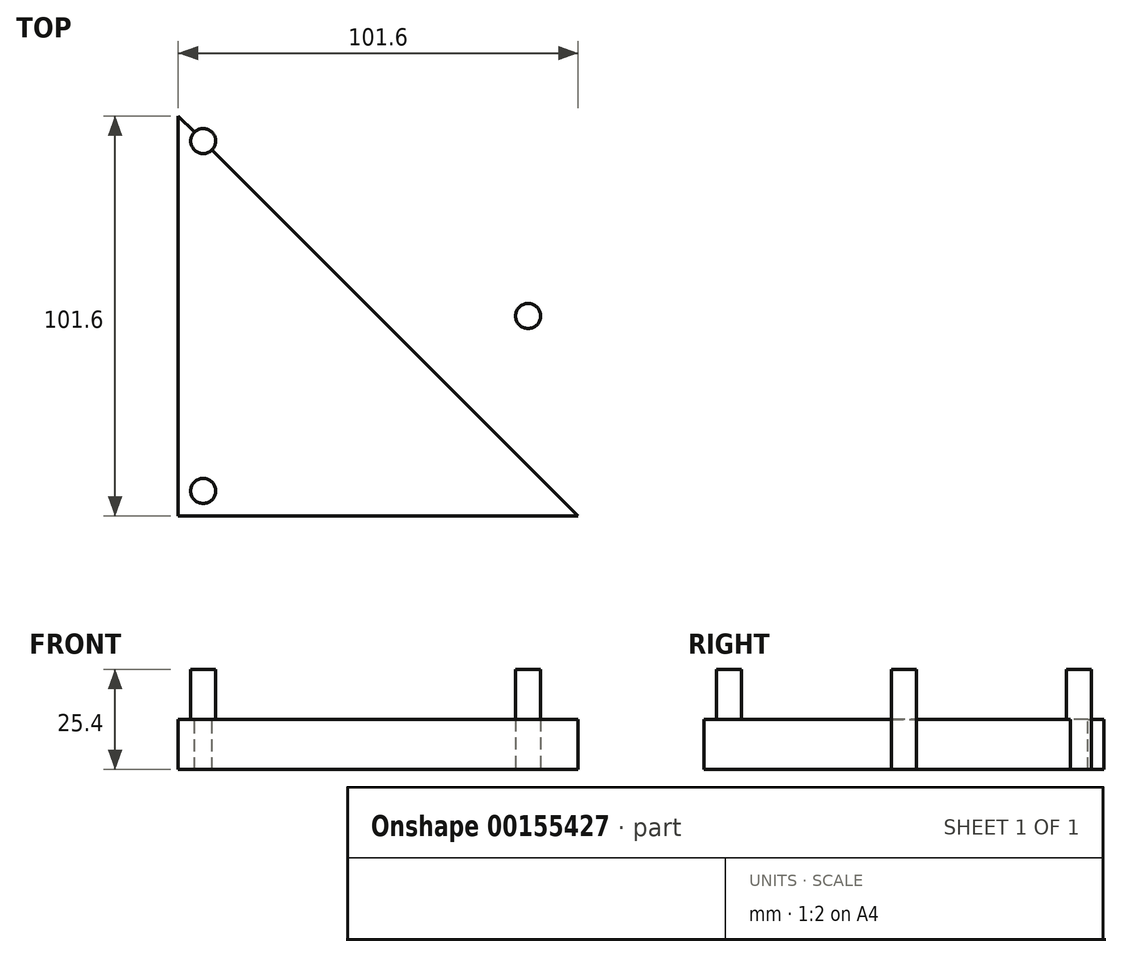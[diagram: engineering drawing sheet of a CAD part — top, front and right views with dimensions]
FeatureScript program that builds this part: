
annotation { "Feature Type Name" : "Feature", "Feature Type Description" : "" }
export const myFeature = defineFeature(function(context is Context, id is Id, definition is map)
    precondition{}
    {
        {
            var Q0;
            Q0=qCreatedBy(makeId("Top.planeOp"),FACE);
            var sketch = newSketch(context, id + "F0", { "sketchPlane" : qUnion([Q0])});
            skLineSegment(sketch, "E0.bottom", {"start": v(0, 0) * mm, "end": v(-101.6, 0) * mm});
            skLineSegment(sketch, "E0.top", {"start": v(0, -101.6) * mm, "end": v(-101.6, -101.6) * mm});
            skLineSegment(sketch, "E0.left", {"start": v(0, 0) * mm, "end": v(0, -101.6) * mm});
            skLineSegment(sketch, "E0.right", {"start": v(-101.6, 0) * mm, "end": v(-101.6, -101.6) * mm});
            skSolve(sketch);
        }
        {
            var Q0;
            Q0=makeQuery(id+"F0.imprint","IMPRINT",FACE,{"disambiguationData":[TD([[makeQuery(id+"F0.imprint","IMPRINT",EDGE,{"derivedFrom":sQuery(id+"F0.wireOp",EDGE,"E0.bottom")}),1.0]])]});
            extrude(context, id + "F1", {"entities" : qUnion([Q0]), "depth" : 12.7 * mm});
        }
        {
            var Q0;
            Q0=makeQuery(id+"F1.opExtrude","CAP_FACE",FACE,{"disambiguationData":[OSD([sQuery(id+"F0.wireOp",EDGE,"E0.bottom"),sQuery(id+"F0.wireOp",EDGE,"E0.top"),sQuery(id+"F0.wireOp",EDGE,"E0.left"),sQuery(id+"F0.wireOp",EDGE,"E0.right")])],"isStart":false});
            var sketch = newSketch(context, id + "F2", { "sketchPlane" : qUnion([Q0])});
            skLineSegment(sketch, "E1.bottom", {"start": v(-101.6, -101.6) * mm, "end": v(-88.9, -101.6) * mm});
            skLineSegment(sketch, "E1.top", {"start": v(-101.6, -88.9) * mm, "end": v(-88.9, -88.9) * mm});
            skLineSegment(sketch, "E1.left", {"start": v(-101.6, -101.6) * mm, "end": v(-101.6, -88.9) * mm});
            skLineSegment(sketch, "E1.right", {"start": v(-88.9, -101.6) * mm, "end": v(-88.9, -88.9) * mm});
            skLineSegment(sketch, "E2", {"start": v(-101.6, -88.9) * mm, "end": v(-88.9, -101.6) * mm});
            skLineSegment(sketch, "E3", {"start": v(-101.6, -101.6) * mm, "end": v(-88.9, -88.9) * mm});
            skPoint(sketch, "E4", {"position": v(-95.25, -95.25) * mm});
            skPoint(sketch, "E5.1.0.0", {"position": v(-69.85, -95.25) * mm});
            skPoint(sketch, "E5.2.0.0", {"position": v(-44.45, -95.25) * mm});
            skLineSegment(sketch, "E5.direction1", {"start": v(-95.25, -95.25) * mm, "end": v(-69.85, -95.25) * mm, "construction": true});
            skLineSegment(sketch, "E6.bottom", {"start": v(-101.6, 0) * mm, "end": v(-88.9, 0) * mm});
            skLineSegment(sketch, "E6.top", {"start": v(-101.6, -12.7) * mm, "end": v(-88.9, -12.7) * mm});
            skLineSegment(sketch, "E6.left", {"start": v(-101.6, 0) * mm, "end": v(-101.6, -12.7) * mm});
            skLineSegment(sketch, "E6.right", {"start": v(-88.9, 0) * mm, "end": v(-88.9, -12.7) * mm});
            skPoint(sketch, "E7", {"position": v(-95.25, -6.35) * mm});
            skPoint(sketch, "E7.positionSnap0", {"position": v(-95.25, -12.7) * mm});
            skPoint(sketch, "E7.positionSnap1", {"position": v(-101.6, -6.35) * mm});
            skCircle(sketch, "E8", {"center": v(-95.25, -95.25) * mm, "radius": 3.18 * mm});
            skCircle(sketch, "E9", {"center": v(-95.25, -6.35) * mm, "radius": 3.18 * mm});
            skSolve(sketch);
        }
        {
            var Q0;
            {var subQ0=sQuery(id+"F2.wireOp",EDGE,"E3");var subQ1=sQuery(id+"F2.wireOp",EDGE,"E2");var subQ2=makeQuery(id+"F2.imprint","INTERSECT",VERTEX,{"derivedFrom":[subQ1,subQ0]});Q0=makeQuery(id+"F2.imprint","IMPRINT",FACE,{"disambiguationData":[TD([[makeQuery(id+"F2.imprint","IMPRINT",EDGE,{"disambiguationData":[TD([[subQ2,-1.0]])],"derivedFrom":subQ1}),-1.0]])]});}
            var Q1;
            {var subQ0=sQuery(id+"F2.wireOp",EDGE,"E8");var subQ1=sQuery(id+"F2.wireOp",EDGE,"E2");var subQ2=makeQuery(id+"F2.imprint","INTERSECT",VERTEX,{"disambiguationData":[OD(0.0)],"derivedFrom":[subQ1,subQ0]});Q1=makeQuery(id+"F2.imprint","IMPRINT",FACE,{"disambiguationData":[TD([[makeQuery(id+"F2.imprint","IMPRINT",EDGE,{"disambiguationData":[TD([[subQ2,-1.0]])],"derivedFrom":subQ1}),1.0]])]});}
            var Q2;
            {var subQ0=sQuery(id+"F2.wireOp",EDGE,"E3");var subQ1=sQuery(id+"F2.wireOp",EDGE,"E2");var subQ2=makeQuery(id+"F2.imprint","INTERSECT",VERTEX,{"derivedFrom":[subQ1,subQ0]});Q2=makeQuery(id+"F2.imprint","IMPRINT",FACE,{"disambiguationData":[TD([[makeQuery(id+"F2.imprint","IMPRINT",EDGE,{"disambiguationData":[TD([[subQ2,-1.0]])],"derivedFrom":subQ1}),1.0]])]});}
            var Q3;
            {var subQ0=sQuery(id+"F2.wireOp",EDGE,"E8");var subQ1=sQuery(id+"F2.wireOp",EDGE,"E2");var subQ2=makeQuery(id+"F2.imprint","INTERSECT",VERTEX,{"disambiguationData":[OD(0.0)],"derivedFrom":[subQ1,subQ0]});Q3=makeQuery(id+"F2.imprint","IMPRINT",FACE,{"disambiguationData":[TD([[makeQuery(id+"F2.imprint","IMPRINT",EDGE,{"disambiguationData":[TD([[subQ2,-1.0]])],"derivedFrom":subQ1}),-1.0]])]});}
            var Q4;
            Q4=makeQuery(id+"F2.imprint","IMPRINT",FACE,{"disambiguationData":[TD([[makeQuery(id+"F2.imprint","IMPRINT",EDGE,{"derivedFrom":sQuery(id+"F2.wireOp",EDGE,"E9")}),1.0]])]});
            extrude(context, id + "F3", {"entities" : qUnion([Q0, Q1, Q2, Q3, Q4]), "operationType" : NewBodyOperationType.ADD, "depth" : 12.7 * mm});
        }
        {
            var Q0;
            Q0=makeQuery(id+"F1.opExtrude","CAP_FACE",FACE,{"disambiguationData":[OSD([sQuery(id+"F0.wireOp",EDGE,"E0.bottom"),sQuery(id+"F0.wireOp",EDGE,"E0.top"),sQuery(id+"F0.wireOp",EDGE,"E0.left"),sQuery(id+"F0.wireOp",EDGE,"E0.right")])],"isStart":false});
            var sketch = newSketch(context, id + "F4", { "sketchPlane" : qUnion([Q0])});
            skLineSegment(sketch, "E10", {"start": v(0, -50.8) * mm, "end": v(-12.7, -50.8) * mm});
            skPoint(sketch, "E10.endSnap0", {"position": v(0, -50.8) * mm});
            skCircle(sketch, "E11", {"center": v(-12.7, -50.8) * mm, "radius": 3.18 * mm});
            skSolve(sketch);
        }
        {
            var Q0;
            Q0=makeQuery(id+"F4.imprint","IMPRINT",FACE,{"disambiguationData":[TD([[makeQuery(id+"F4.imprint","IMPRINT",EDGE,{"derivedFrom":sQuery(id+"F4.wireOp",EDGE,"E11")}),1.0]])]});
            extrude(context, id + "F5", {"entities" : qUnion([Q0]), "operationType" : NewBodyOperationType.ADD, "depth" : 12.7 * mm});
        }
        {
            var Q0;
            Q0=makeQuery(id+"F1.opExtrude","CAP_FACE",FACE,{"disambiguationData":[OSD([sQuery(id+"F0.wireOp",EDGE,"E0.bottom"),sQuery(id+"F0.wireOp",EDGE,"E0.top"),sQuery(id+"F0.wireOp",EDGE,"E0.left"),sQuery(id+"F0.wireOp",EDGE,"E0.right")])],"isStart":false});
            var sketch = newSketch(context, id + "F6", { "sketchPlane" : qUnion([Q0])});
            skLineSegment(sketch, "E12", {"start": v(-101.6, -101.6) * mm, "end": v(0, 0) * mm});
            skLineSegment(sketch, "E13", {"start": v(0, 0) * mm, "end": v(0, -101.6) * mm});
            skLineSegment(sketch, "E14", {"start": v(0, -101.6) * mm, "end": v(-101.6, 0) * mm});
            skCircle(sketch, "E15", {"center": v(-50.8, -50.8) * mm, "radius": 31.75 * mm});
            skSolve(sketch);
        }
        {
            var Q0;
            {var subQ0=sQuery(id+"F6.wireOp",EDGE,"E15");var subQ1=sQuery(id+"F6.wireOp",EDGE,"E12");var subQ2=makeQuery(id+"F6.imprint","INTERSECT",VERTEX,{"disambiguationData":[OD(0.0)],"derivedFrom":[subQ1,subQ0]});Q0=makeQuery(id+"F6.imprint","IMPRINT",FACE,{"disambiguationData":[TD([[makeQuery(id+"F6.imprint","IMPRINT",EDGE,{"disambiguationData":[TD([[subQ2,-1.0]])],"derivedFrom":subQ1}),1.0]])]});}
            var Q1;
            {var subQ0=sQuery(id+"F6.wireOp",EDGE,"E14");var subQ1=sQuery(id+"F6.wireOp",EDGE,"E12");var subQ2=makeQuery(id+"F6.imprint","INTERSECT",VERTEX,{"derivedFrom":[subQ1,subQ0]});Q1=makeQuery(id+"F6.imprint","IMPRINT",FACE,{"disambiguationData":[TD([[makeQuery(id+"F6.imprint","IMPRINT",EDGE,{"disambiguationData":[TD([[subQ2,-1.0]])],"derivedFrom":subQ1}),1.0]])]});}
            var Q2;
            {var subQ0=sQuery(id+"F6.wireOp",EDGE,"E14");var subQ1=sQuery(id+"F6.wireOp",EDGE,"E12");var subQ2=makeQuery(id+"F6.imprint","INTERSECT",VERTEX,{"derivedFrom":[subQ1,subQ0]});Q2=makeQuery(id+"F6.imprint","IMPRINT",FACE,{"disambiguationData":[TD([[makeQuery(id+"F6.imprint","IMPRINT",EDGE,{"disambiguationData":[TD([[subQ2,-1.0]])],"derivedFrom":subQ1}),-1.0]])]});}
            var Q3;
            {var subQ0=sQuery(id+"F6.wireOp",EDGE,"E15");var subQ1=sQuery(id+"F6.wireOp",EDGE,"E12");var subQ2=makeQuery(id+"F6.imprint","INTERSECT",VERTEX,{"disambiguationData":[OD(0.0)],"derivedFrom":[subQ1,subQ0]});Q3=makeQuery(id+"F6.imprint","IMPRINT",FACE,{"disambiguationData":[TD([[makeQuery(id+"F6.imprint","IMPRINT",EDGE,{"disambiguationData":[TD([[subQ2,-1.0]])],"derivedFrom":subQ1}),-1.0]])]});}
            extrude(context, id + "F7", {"entities" : qUnion([Q0, Q1, Q2, Q3]), "operationType" : NewBodyOperationType.REMOVE, "oppositeDirection" : true, "depth" : 25.4 * mm});
        }
    });
